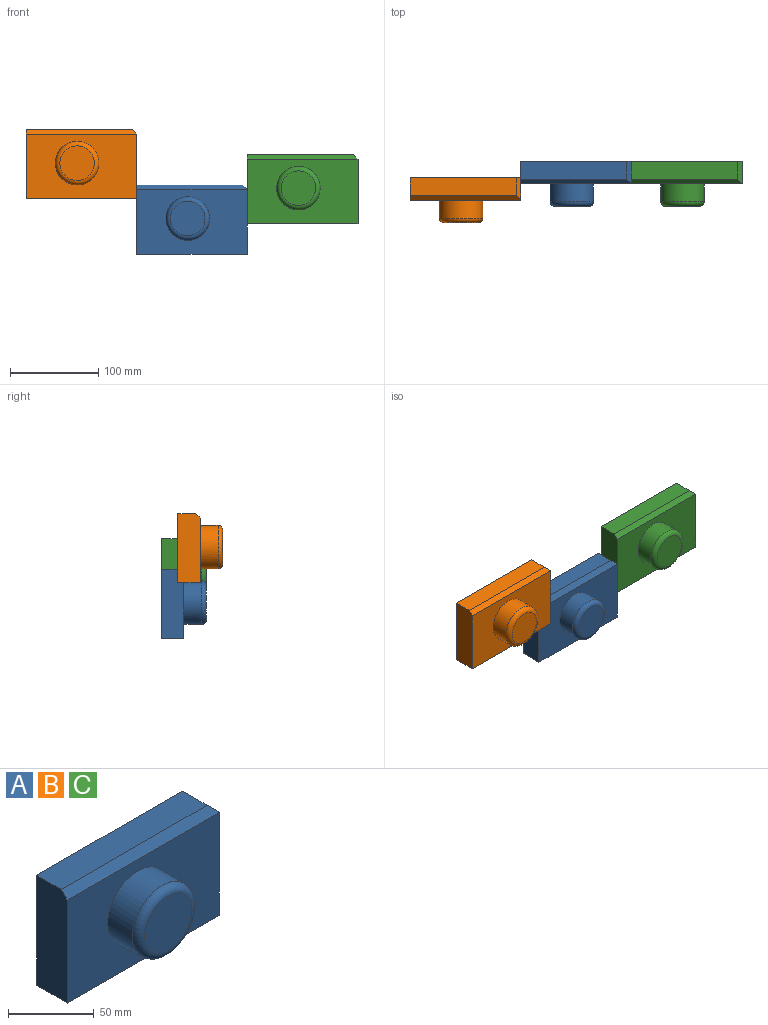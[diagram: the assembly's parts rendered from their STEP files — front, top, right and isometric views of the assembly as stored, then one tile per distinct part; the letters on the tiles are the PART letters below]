
ASSEMBLY  parts=3 mates=2
PART A: 11 faces, bbox 125.6x50.8x78.7 mm
  f0: plane 120.52x20.32mm, normal (0,0,1), area 2448.9mm2, adj f1,f5,f6,f7
  f1: plane 78.66x25.4mm, normal (-1,0,0), area 1985.1mm2, adj f0,f2,f4,f5,f7
  f2: plane 125.6x25.4mm, normal (0,0,-1), area 3190.2mm2, adj f1,f3,f4,f5
  f3: plane 73.58x25.4mm, normal (1,0,0), area 1868.9mm2, adj f2,f4,f5,f6
  f4: plane 125.6x73.58mm, normal (0,-1,0), area 7331.9mm2, adj f1,f2,f3,f7,f8
  f5: plane 125.6x78.66mm, normal (0,1,0), area 9866.5mm2, adj f0,f1,f2,f3,f6
  f6: plane 25.4x5.08mm, normal (0.71,0,0.71), area 164.2mm2, adj f0,f3,f5,f7
  f7: plane 125.6x5.08mm, normal (0,-0.71,0.71), area 884.1mm2, adj f0,f1,f4,f6
  f8: cylinder r=24.65mm len=49.31mm, axis (0,1,0), area 3147.7mm2, adj f4,f10
  f9: plane 39.15x39.15mm, normal (0,-1,0), area 1203.7mm2, adj f10
  f10: torus R=19.57mm, axis (0,-1,0), area 1143.5mm2, adj f8,f9
PART B: same geometry as A
PART C: same geometry as A
PLACE A t=(32.71,38.13,-155.48)mm
PLACE B t=(-92.89,19.55,-92.59)mm
PLACE C t=(158.31,38.06,-120.99)mm
MATE planar A.f3 <-> C.f1  axis (1,0,0) through (100.31,25.43,-122.51)mm
MATE planar B.f3 <-> A.f1  axis (1,0,0) through (-25.28,-5.85,-59.62)mm
